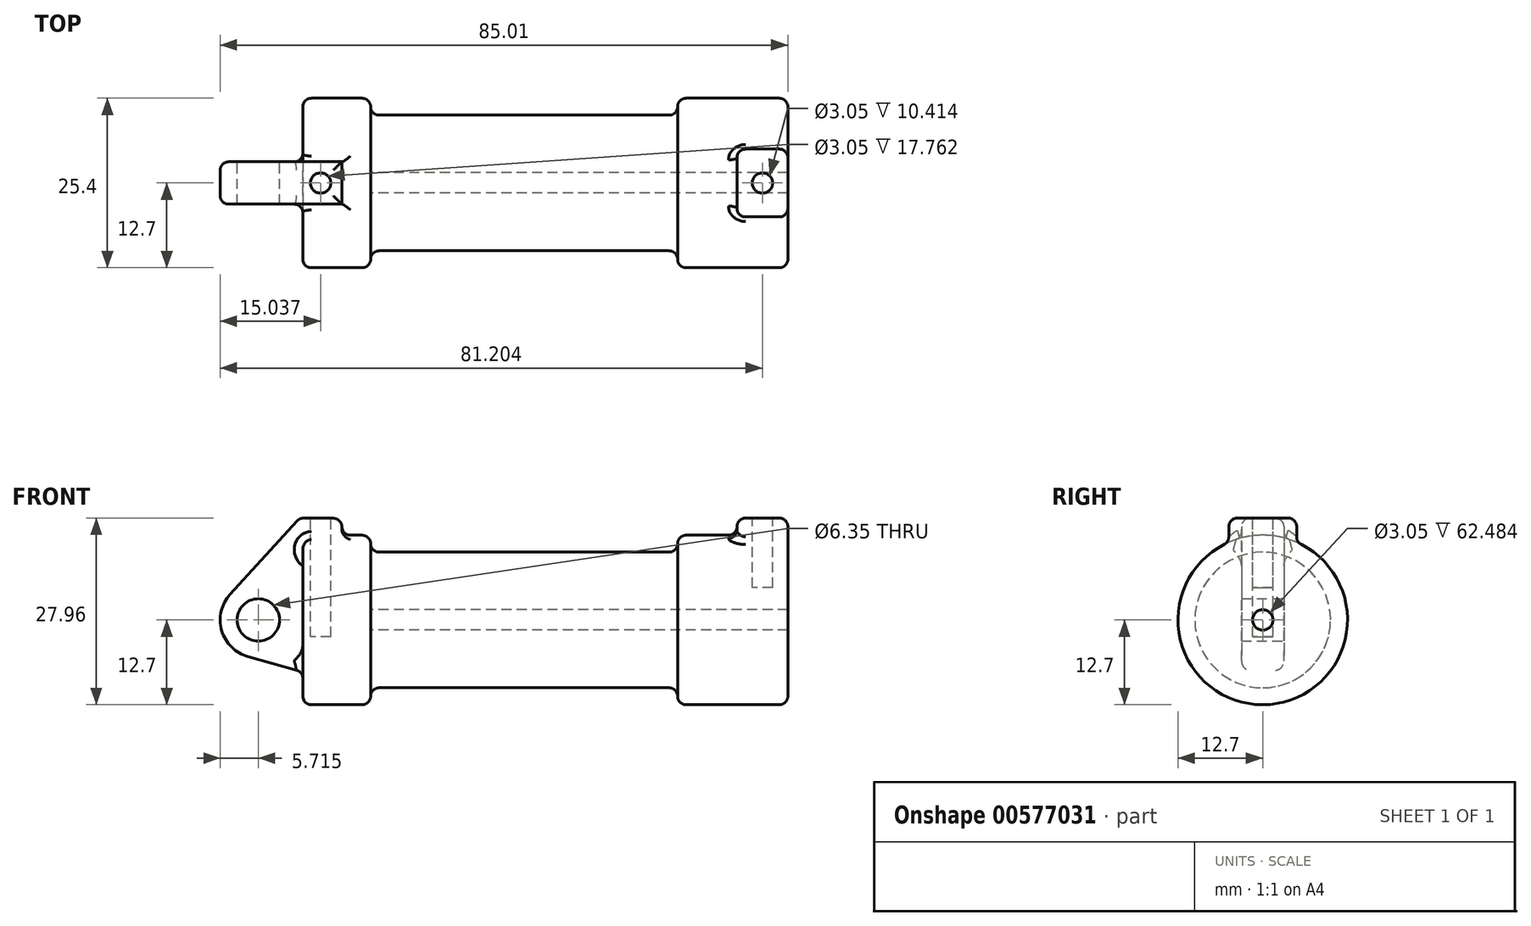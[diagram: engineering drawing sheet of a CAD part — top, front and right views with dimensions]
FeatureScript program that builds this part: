
annotation { "Feature Type Name" : "Feature", "Feature Type Description" : "" }
export const myFeature = defineFeature(function(context is Context, id is Id, definition is map)
    precondition{}
    {
        {
            var Q0;
            Q0=qCreatedBy(makeId("Front.planeOp"),FACE);
            var sketch = newSketch(context, id + "F0", { "sketchPlane" : qUnion([Q0])});
            skLineSegment(sketch, "E0", {"start": v(0, 0) * mm, "end": v(0, 12.7) * mm});
            skLineSegment(sketch, "E1", {"start": v(0, 12.7) * mm, "end": v(10.16, 12.7) * mm});
            skLineSegment(sketch, "E2", {"start": v(10.16, 12.7) * mm, "end": v(10.16, 10.16) * mm});
            skLineSegment(sketch, "E3", {"start": v(10.16, 10.16) * mm, "end": v(56.13, 10.16) * mm});
            skLineSegment(sketch, "E4", {"start": v(56.13, 10.16) * mm, "end": v(56.13, 12.7) * mm});
            skLineSegment(sketch, "E5", {"start": v(56.13, 12.7) * mm, "end": v(66.3, 12.7) * mm});
            skLineSegment(sketch, "E6", {"start": v(66.3, 12.7) * mm, "end": v(66.3, 0) * mm});
            skLineSegment(sketch, "E7", {"start": v(66.3, 0) * mm, "end": v(0, 0) * mm});
            skLineSegment(sketch, "E8", {"start": v(5.84, 15.24) * mm, "end": v(-0.5, 15.24) * mm});
            skLineSegment(sketch, "E9", {"start": v(-0.5, 15.24) * mm, "end": v(-10.88, 3.85) * mm});
            skLineSegment(sketch, "E10", {"start": v(0, 0) * mm, "end": v(-6.65, 0) * mm});
            skCircle(sketch, "E11", {"center": v(-6.65, 0) * mm, "radius": 5.72 * mm});
            skCircle(sketch, "E12", {"center": v(-6.65, 0) * mm, "radius": 3.18 * mm});
            skLineSegment(sketch, "E13", {"start": v(5.84, 15.24) * mm, "end": v(5.84, -9.4) * mm});
            skLineSegment(sketch, "E14", {"start": v(5.84, -9.4) * mm, "end": v(-8.18, -5.5) * mm});
            skSolve(sketch);
        }
        {
            var Q0;
            {var subQ1=sQuery(id+"F0.wireOp",EDGE,"E0");Q0=makeQuery(id+"F0.imprint","IMPRINT",FACE,{"disambiguationData":[TD([[makeQuery(id+"F0.imprint","IMPRINT",EDGE,{"derivedFrom":subQ1}),1.0]])]});}
            var Q1;
            {var subQ0=sQuery(id+"F0.wireOp",EDGE,"E14");Q1=makeQuery(id+"F0.imprint","IMPRINT",FACE,{"disambiguationData":[TD([[makeQuery(id+"F0.imprint","IMPRINT",EDGE,{"derivedFrom":subQ0}),-1.0]])]});}
            var Q2;
            {var subQ5=sQuery(id+"F0.wireOp",EDGE,"E12");Q2=makeQuery(id+"F0.imprint","IMPRINT",FACE,{"disambiguationData":[TD([[makeQuery(id+"F0.imprint","IMPRINT",EDGE,{"derivedFrom":subQ5}),-1.0]])]});}
            var Q3;
            {var subQ0=sQuery(id+"F0.wireOp",EDGE,"E0");Q3=makeQuery(id+"F0.imprint","IMPRINT",FACE,{"disambiguationData":[TD([[makeQuery(id+"F0.imprint","IMPRINT",EDGE,{"derivedFrom":subQ0}),-1.0]])]});}
            extrude(context, id + "F1", {"entities" : qUnion([Q0, Q1, Q2, Q3]), "endBound" : BoundingType.SYMMETRIC, "depth" : 6.35 * mm, "offsetDistance" : 25.4 * mm});
        }
        {
            var Q0;
            {var subQ0=sQuery(id+"F0.wireOp",EDGE,"E0");Q0=makeQuery(id+"F0.imprint","IMPRINT",FACE,{"disambiguationData":[TD([[makeQuery(id+"F0.imprint","IMPRINT",EDGE,{"derivedFrom":subQ0}),-1.0]])]});}
            var Q1;
            {var subQ0=sQuery(id+"F0.wireOp",EDGE,"E2");Q1=makeQuery(id+"F0.imprint","IMPRINT",FACE,{"disambiguationData":[TD([[makeQuery(id+"F0.imprint","IMPRINT",EDGE,{"derivedFrom":subQ0}),-1.0]])]});}
            var Q2;
            Q2=sQuery(id+"F0.wireOp",EDGE,"E7");
            revolve(context, id + "F2", {"operationType" : NewBodyOperationType.ADD, "entities" : qUnion([Q0, Q1]), "axis" : qUnion([Q2]), "revolveType" : RevolveType.FULL, "oppositeDirection" : true});
        }
        {
            var Q0;
            Q0=makeQuery(id+"F2.opRevolve","SWEPT_FACE",FACE,{"disambiguationData":[OSD([sQuery(id+"F0.wireOp",EDGE,"E6")])]});
            var sketch = newSketch(context, id + "F3", { "sketchPlane" : qUnion([Q0])});
            skCircle(sketch, "E15", {"center": v(0, 0) * mm, "radius": 1.52 * mm});
            skCircle(sketch, "E16", {"center": v(0, 0) * mm, "radius": 5.08 * mm});
            skLineSegment(sketch, "E17.top", {"start": v(-5.08, 15.26) * mm, "end": v(5.08, 15.26) * mm});
            skLineSegment(sketch, "E17.left", {"start": v(-5.08, 0) * mm, "end": v(-5.08, 15.26) * mm});
            skLineSegment(sketch, "E17.right", {"start": v(5.08, 0.02) * mm, "end": v(5.08, 15.26) * mm});
            skSolve(sketch);
        }
        {
            var Q0;
            {var subQ0=sQuery(id+"F3.wireOp",EDGE,"E17.top");Q0=makeQuery(id+"F3.imprint","IMPRINT",FACE,{"disambiguationData":[TD([[makeQuery(id+"F3.imprint","IMPRINT",EDGE,{"derivedFrom":subQ0}),-1.0]])]});}
            var Q1;
            {var subQ0=sQuery(id+"F3.wireOp",EDGE,"E17.left");var subQ1=sQuery(id+"F3.wireOp",EDGE,"E16");var subQ2=makeQuery(id+"F3.imprint","INTERSECT",VERTEX,{"derivedFrom":[subQ1,subQ0]});Q1=makeQuery(id+"F3.imprint","IMPRINT",FACE,{"disambiguationData":[TD([[makeQuery(id+"F3.imprint","IMPRINT",EDGE,{"disambiguationData":[TD([[subQ2,1.0]])],"derivedFrom":subQ1}),-1.0]])]});}
            var Q2;
            Q2=makeQuery(id+"F3.imprint","IMPRINT",FACE,{"disambiguationData":[TD([[makeQuery(id+"F3.imprint","IMPRINT",EDGE,{"derivedFrom":sQuery(id+"F3.wireOp",EDGE,"E15")}),-1.0]])]});
            extrude(context, id + "F4", {"entities" : qUnion([Q0, Q1, Q2]), "operationType" : NewBodyOperationType.ADD, "depth" : 6.35 * mm, "offsetDistance" : 25.4 * mm});
        }
        {
            var Q0;
            Q0=makeQuery(id+"F4.opExtrude","CAP_FACE",FACE,{"disambiguationData":[OSD([sQuery(id+"F3.wireOp",EDGE,"E15"),sQuery(id+"F3.wireOp",EDGE,"E16"),sQuery(id+"F3.wireOp",EDGE,"E17.top"),sQuery(id+"F3.wireOp",EDGE,"E17.left"),sQuery(id+"F3.wireOp",EDGE,"E17.right")])],"isStart":true});
            extrude(context, id + "F5", {"entities" : qUnion([Q0]), "operationType" : NewBodyOperationType.ADD, "depth" : 1.27 * mm, "offsetDistance" : 25.4 * mm});
        }
        {
            var Q0;
            Q0=makeQuery(id+"F4.boolean.opBoolean","SPLIT",FACE,{"disambiguationData":[TD([makeQuery(id+"F4.opExtrude","SWEPT_FACE",FACE,{"disambiguationData":[OSD([sQuery(id+"F3.wireOp",EDGE,"E15")])]})])],"derivedFrom":makeQuery(id+"F2.opRevolve","SWEPT_FACE",FACE,{"disambiguationData":[OSD([sQuery(id+"F0.wireOp",EDGE,"E6")])]})});
            var Q1;
            Q1=makeQuery(id+"F2.opRevolve","SWEPT_FACE",FACE,{"disambiguationData":[OSD([sQuery(id+"F0.wireOp",EDGE,"E2")])]});
            extrude(context, id + "F6", {"entities" : qUnion([Q0]), "operationType" : NewBodyOperationType.REMOVE, "endBound" : BoundingType.UP_TO_SURFACE, "oppositeDirection" : true, "depth" : 25.4 * mm, "endBoundEntityFace" : qUnion([Q1]), "offsetDistance" : 25.4 * mm});
        }
        {
            var Q0;
            {var subQ0=sQuery(id+"F3.wireOp",EDGE,"E17.top");Q0=makeQuery(id+"F5.boolean.opBoolean","MERGE",FACE,{"derivedFrom":[makeQuery(id+"F4.opExtrude","SWEPT_FACE",FACE,{"disambiguationData":[OSD([subQ0])]}),makeQuery(id+"F5.opExtrude","SWEPT_FACE",FACE,{"disambiguationData":[OSD([subQ0])]})]});}
            var sketch = newSketch(context, id + "F7", { "sketchPlane" : qUnion([Q0])});
            skLineSegment(sketch, "E18.0.0", {"start": v(5.84, 3.18) * mm, "end": v(-0.5, 3.18) * mm});
            skLineSegment(sketch, "E18.0.1", {"start": v(-0.5, 3.17) * mm, "end": v(-0.5, -3.18) * mm});
            skLineSegment(sketch, "E18.0.2", {"start": v(-0.5, -3.18) * mm, "end": v(5.84, -3.18) * mm});
            skLineSegment(sketch, "E18.0.3", {"start": v(5.84, -3.18) * mm, "end": v(5.84, 3.17) * mm});
            skLineSegment(sketch, "E19.0.0", {"start": v(72.64, 5.08) * mm, "end": v(65.02, 5.08) * mm});
            skLineSegment(sketch, "E19.0.1", {"start": v(65.02, 5.08) * mm, "end": v(65.02, -5.08) * mm});
            skLineSegment(sketch, "E19.0.2", {"start": v(65.02, -5.08) * mm, "end": v(72.64, -5.08) * mm});
            skLineSegment(sketch, "E19.0.3", {"start": v(72.64, -5.08) * mm, "end": v(72.64, 5.08) * mm});
            skCircle(sketch, "E20", {"center": v(2.67, 0) * mm, "radius": 1.52 * mm});
            skPoint(sketch, "E20.centerSnap0", {"position": v(2.67, 3.18) * mm});
            skPoint(sketch, "E20.centerSnap1", {"position": v(5.84, 0) * mm});
            skCircle(sketch, "E21", {"center": v(68.83, 0) * mm, "radius": 1.52 * mm});
            skPoint(sketch, "E21.centerSnap0", {"position": v(68.83, 5.08) * mm});
            skPoint(sketch, "E21.centerSnap1", {"position": v(65.02, 0) * mm});
            skSolve(sketch);
        }
        {
            var Q0;
            Q0=makeQuery(id+"F7.imprint","IMPRINT",FACE,{"disambiguationData":[TD([[makeQuery(id+"F7.imprint","IMPRINT",EDGE,{"derivedFrom":sQuery(id+"F7.wireOp",EDGE,"E21")}),1.0]])]});
            extrude(context, id + "F8", {"entities" : qUnion([Q0]), "operationType" : NewBodyOperationType.REMOVE, "oppositeDirection" : true, "depth" : 10.4 * mm, "offsetDistance" : 25.4 * mm});
        }
        {
            var Q0;
            Q0=makeQuery(id+"F7.imprint","IMPRINT",FACE,{"disambiguationData":[TD([[makeQuery(id+"F7.imprint","IMPRINT",EDGE,{"derivedFrom":sQuery(id+"F7.wireOp",EDGE,"E20")}),1.0]])]});
            extrude(context, id + "F9", {"entities" : qUnion([Q0]), "operationType" : NewBodyOperationType.REMOVE, "oppositeDirection" : true, "depth" : 17.78 * mm, "offsetDistance" : 25.4 * mm});
        }
        {
            var Q0;
            Q0=makeQuery(id+"F2.opRevolve","SWEPT_EDGE",EDGE,{"disambiguationData":[OSD([sQuery(id+"F0.wireOp",EDGE,"E4"),sQuery(id+"F0.wireOp",EDGE,"E5")])]});
            var Q1;
            Q1=makeQuery(id+"F2.opRevolve","SWEPT_FACE",FACE,{"disambiguationData":[OSD([sQuery(id+"F0.wireOp",EDGE,"E5")])]});
            var Q2;
            {var subQ0=sQuery(id+"F3.wireOp",EDGE,"E17.right");Q2=makeQuery(id+"F5.boolean.opBoolean","MERGE",FACE,{"derivedFrom":[makeQuery(id+"F4.opExtrude","SWEPT_FACE",FACE,{"disambiguationData":[OSD([subQ0])]}),makeQuery(id+"F5.opExtrude","SWEPT_FACE",FACE,{"disambiguationData":[OSD([subQ0])]})]});}
            var Q3;
            Q3=makeQuery(id+"F4.opExtrude","SWEPT_FACE",FACE,{"disambiguationData":[OSD([sQuery(id+"F3.wireOp",EDGE,"E16")])]});
            var Q4;
            Q4=makeQuery(id+"F4.opExtrude","CAP_EDGE",EDGE,{"disambiguationData":[OSD([sQuery(id+"F3.wireOp",EDGE,"E17.left")])],"isStart":false});
            var Q5;
            Q5=makeQuery(id+"F5.opExtrude","CAP_EDGE",EDGE,{"disambiguationData":[OSD([sQuery(id+"F3.wireOp",EDGE,"E17.left")])],"isStart":false});
            var Q6;
            {var subQ0=sQuery(id+"F3.wireOp",EDGE,"E17.left");var subQ1=sQuery(id+"F3.wireOp",EDGE,"E17.top");Q6=makeQuery(id+"F5.boolean.opBoolean","MERGE",EDGE,{"derivedFrom":[makeQuery(id+"F4.opExtrude","SWEPT_EDGE",EDGE,{"disambiguationData":[OSD([subQ1,subQ0])]}),makeQuery(id+"F5.opExtrude","SWEPT_EDGE",EDGE,{"disambiguationData":[OSD([subQ1,subQ0])]})]});}
            var Q7;
            Q7=makeQuery(id+"F4.opExtrude","CAP_EDGE",EDGE,{"disambiguationData":[OSD([sQuery(id+"F3.wireOp",EDGE,"E17.top")])],"isStart":false});
            var Q8;
            Q8=makeQuery(id+"F5.opExtrude","CAP_EDGE",EDGE,{"disambiguationData":[OSD([sQuery(id+"F3.wireOp",EDGE,"E17.top")])],"isStart":false});
            var Q9;
            Q9=makeQuery(id+"F2.opRevolve","SWEPT_FACE",FACE,{"disambiguationData":[OSD([sQuery(id+"F0.wireOp",EDGE,"E3")])]});
            var Q10;
            Q10=makeQuery(id+"F2.opRevolve","SWEPT_EDGE",EDGE,{"disambiguationData":[OSD([sQuery(id+"F0.wireOp",EDGE,"E1"),sQuery(id+"F0.wireOp",EDGE,"E2")])]});
            var Q11;
            Q11=makeQuery(id+"F2.opRevolve","SWEPT_FACE",FACE,{"disambiguationData":[OSD([sQuery(id+"F0.wireOp",EDGE,"E1")])]});
            var Q12;
            Q12=makeQuery(id+"F1.opExtrude","SWEPT_FACE",FACE,{"disambiguationData":[OSD([sQuery(id+"F0.wireOp",EDGE,"E14")])]});
            var Q13;
            Q13=makeQuery(id+"F1.opExtrude","SWEPT_FACE",FACE,{"disambiguationData":[OSD([sQuery(id+"F0.wireOp",EDGE,"E11")])]});
            var Q14;
            Q14=makeQuery(id+"F1.opExtrude","CAP_EDGE",EDGE,{"disambiguationData":[OSD([sQuery(id+"F0.wireOp",EDGE,"E8")])],"isStart":true});
            var Q15;
            Q15=makeQuery(id+"F1.opExtrude","SWEPT_EDGE",EDGE,{"disambiguationData":[OSD([sQuery(id+"F0.wireOp",EDGE,"E8"),sQuery(id+"F0.wireOp",EDGE,"E9")])]});
            var Q16;
            Q16=makeQuery(id+"F1.opExtrude","CAP_EDGE",EDGE,{"disambiguationData":[OSD([sQuery(id+"F0.wireOp",EDGE,"E8")])],"isStart":false});
            var Q17;
            Q17=makeQuery(id+"F1.opExtrude","SWEPT_EDGE",EDGE,{"disambiguationData":[OSD([sQuery(id+"F0.wireOp",EDGE,"E8"),sQuery(id+"F0.wireOp",EDGE,"E13")])]});
            fillet(context, id + "F10", {"entities" : qUnion([Q0, Q1, Q2, Q3, Q4, Q5, Q6, Q7, Q8, Q9, Q10, Q11, Q12, Q13, Q14, Q15, Q16, Q17]), "radius" : 1.27 * mm, "tangentPropagation" : true, "allowEdgeOverflow" : false});
        }
    });
